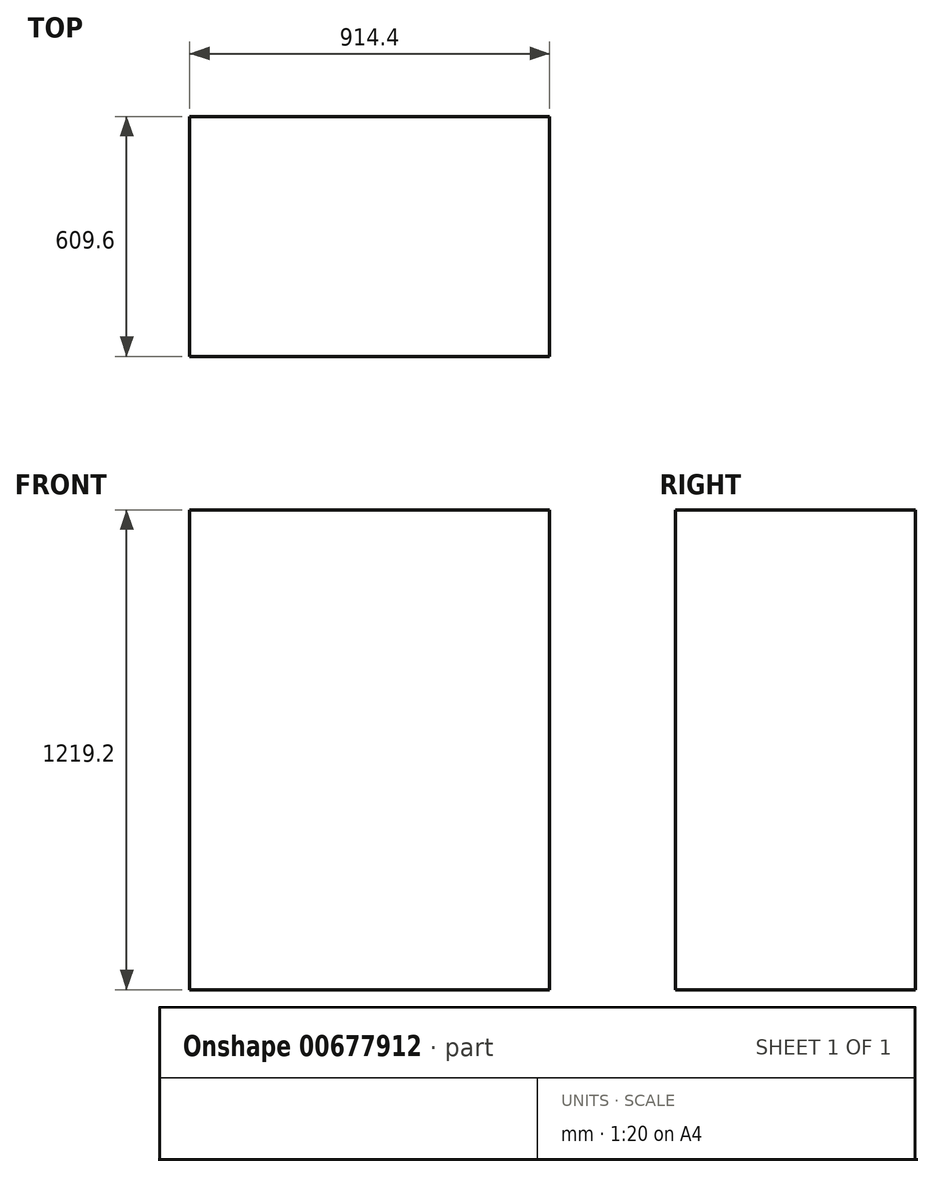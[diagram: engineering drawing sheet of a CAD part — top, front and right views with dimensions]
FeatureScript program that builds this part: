
annotation { "Feature Type Name" : "Feature", "Feature Type Description" : "" }
export const myFeature = defineFeature(function(context is Context, id is Id, definition is map)
    precondition{}
    {
        {
            var Q0;
            Q0=qCreatedBy(makeId("Front.planeOp"),FACE);
            var sketch = newSketch(context, id + "F0", { "sketchPlane" : qUnion([Q0])});
            skLineSegment(sketch, "E0.bottom", {"start": v(-457.2, 609.6) * mm, "end": v(457.2, 609.6) * mm});
            skLineSegment(sketch, "E0.top", {"start": v(-457.2, -609.6) * mm, "end": v(457.2, -609.6) * mm});
            skLineSegment(sketch, "E0.left", {"start": v(-457.2, 609.6) * mm, "end": v(-457.2, -609.6) * mm});
            skLineSegment(sketch, "E0.right", {"start": v(457.2, 609.6) * mm, "end": v(457.2, -609.6) * mm});
            skPoint(sketch, "E0.middle", {"position": v(0, 0) * mm});
            skSolve(sketch);
        }
        {
            var Q0;
            Q0=makeQuery(id+"F0.imprint","IMPRINT",FACE,{"disambiguationData":[TD([[makeQuery(id+"F0.imprint","IMPRINT",EDGE,{"derivedFrom":sQuery(id+"F0.wireOp",EDGE,"E0.bottom")}),-1.0]])]});
            extrude(context, id + "F1", {"entities" : qUnion([Q0]), "depth" : 609.6 * mm, "offsetDistance" : 25.4 * mm});
        }
    });
